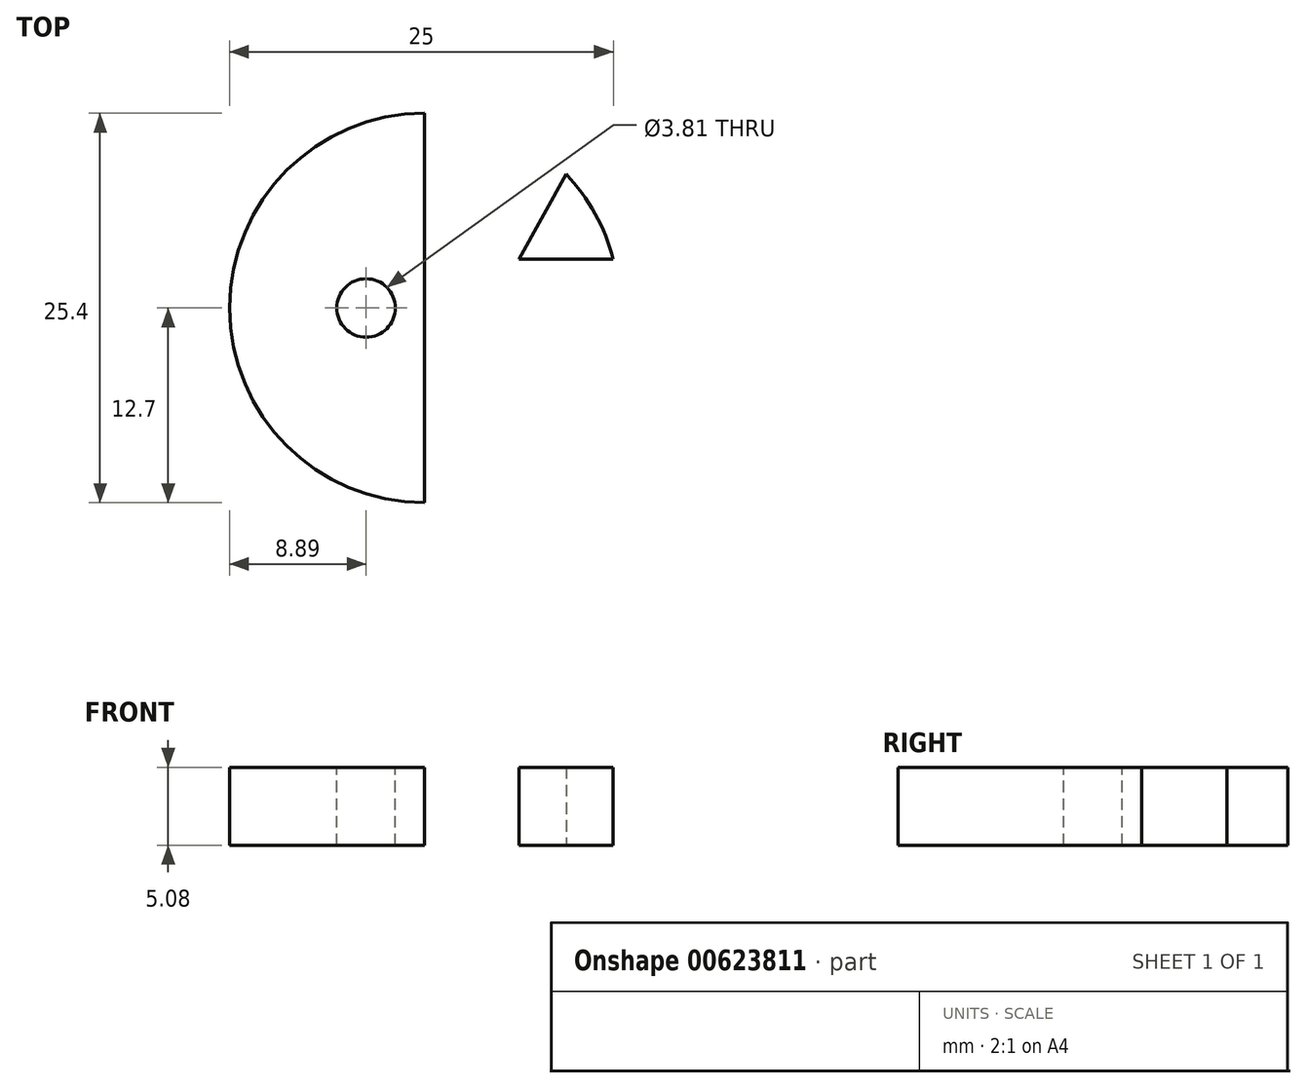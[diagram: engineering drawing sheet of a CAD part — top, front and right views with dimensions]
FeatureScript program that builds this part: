
annotation { "Feature Type Name" : "Feature", "Feature Type Description" : "" }
export const myFeature = defineFeature(function(context is Context, id is Id, definition is map)
    precondition{}
    {
        {
            var Q0;
            Q0=qCreatedBy(makeId("Top.planeOp"),FACE);
            var sketch = newSketch(context, id + "F0", { "sketchPlane" : qUnion([Q0])});
            skCircle(sketch, "E0", {"center": v(0, 0) * mm, "radius": 12.7 * mm});
            skLineSegment(sketch, "E1", {"start": v(0, 0) * mm, "end": v(0, 12.7) * mm});
            skLineSegment(sketch, "E2", {"start": v(0, 6.35) * mm, "end": v(0, 0) * mm});
            skLineSegment(sketch, "E3", {"start": v(0, 3.18) * mm, "end": v(0, 6.35) * mm});
            skLineSegment(sketch, "E4", {"start": v(0, 3.18) * mm, "end": v(12.3, 3.18) * mm});
            skLineSegment(sketch, "E5", {"start": v(-12.7, 0) * mm, "end": v(12.7, 0) * mm});
            skLineSegment(sketch, "E6.MirrorCS", {"start": v(0, -3.18) * mm, "end": v(12.3, -3.18) * mm});
            skLineSegment(sketch, "E7.MirrorCS", {"start": v(0, -6.35) * mm, "end": v(0, 0) * mm});
            skLineSegment(sketch, "E8.MirrorCS", {"start": v(0, 0) * mm, "end": v(0, -12.7) * mm});
            skLineSegment(sketch, "E9", {"start": v(6.15, 3.17) * mm, "end": v(9.22, 8.73) * mm});
            skLineSegment(sketch, "E10.MirrorCS", {"start": v(6.15, -3.17) * mm, "end": v(9.22, -8.73) * mm});
            skSolve(sketch);
        }
        {
            var Q0;
            {var subQ4=sQuery(id+"F0.wireOp",EDGE,"E2");Q0=makeQuery(id+"F0.imprint","IMPRINT",FACE,{"disambiguationData":[TD([[makeQuery(id+"F0.imprint","IMPRINT",EDGE,{"derivedFrom":subQ4}),1.0]])]});}
            var Q1;
            {var subQ1=sQuery(id+"F0.wireOp",EDGE,"E0");var subQ6=sQuery(id+"F0.wireOp",EDGE,"E5");var subQ8=makeQuery(id+"F0.imprint","INTERSECT",VERTEX,{"disambiguationData":[OD(1.0)],"derivedFrom":[subQ1,subQ6]});Q1=makeQuery(id+"F0.imprint","IMPRINT",FACE,{"disambiguationData":[TD([[makeQuery(id+"F0.imprint","IMPRINT",EDGE,{"disambiguationData":[TD([[subQ8,1.0]])],"derivedFrom":subQ1}),1.0]])]});}
            var Q2;
            {var subQ0=sQuery(id+"F0.wireOp",EDGE,"E8.MirrorCS");var subQ4=makeQuery(id+"F0.imprint","IMPRINT",VERTEX,{"derivedFrom":subQ0});Q2=makeQuery(id+"F0.imprint","IMPRINT",FACE,{"disambiguationData":[TD([[makeQuery(id+"F0.imprint","IMPRINT",EDGE,{"disambiguationData":[TD([[subQ4,1.0]])],"derivedFrom":subQ0}),-1.0]])]});}
            var Q3;
            {var subQ1=sQuery(id+"F0.wireOp",EDGE,"E1");Q3=makeQuery(id+"F0.imprint","IMPRINT",FACE,{"disambiguationData":[TD([[makeQuery(id+"F0.imprint","IMPRINT",EDGE,{"derivedFrom":subQ1}),1.0]])]});}
            var Q4;
            {var subQ3=sQuery(id+"F0.wireOp",EDGE,"E9");Q4=makeQuery(id+"F0.imprint","IMPRINT",FACE,{"disambiguationData":[TD([[makeQuery(id+"F0.imprint","IMPRINT",EDGE,{"derivedFrom":subQ3}),-1.0]])]});}
            extrude(context, id + "F1", {"entities" : qUnion([Q0, Q1, Q2, Q3, Q4]), "depth" : 5.08 * mm, "offsetDistance" : 25.4 * mm});
        }
        {
            var Q0;
            Q0=makeQuery(id+"F1.opExtrude","CAP_FACE",FACE,{"disambiguationData":[OSD([sQuery(id+"F0.wireOp",EDGE,"E0"),sQuery(id+"F0.wireOp",EDGE,"E1"),sQuery(id+"F0.wireOp",EDGE,"E3"),sQuery(id+"F0.wireOp",EDGE,"E4"),sQuery(id+"F0.wireOp",EDGE,"E6.MirrorCS"),sQuery(id+"F0.wireOp",EDGE,"E8.MirrorCS"),sQuery(id+"F0.wireOp",EDGE,"E9")])],"isStart":false});
            var sketch = newSketch(context, id + "F2", { "sketchPlane" : qUnion([Q0])});
            skCircle(sketch, "E11", {"center": v(-3.81, 0) * mm, "radius": 1.9 * mm});
            skPoint(sketch, "E12", {"position": v(-3.81, 3.18) * mm});
            skSolve(sketch);
        }
        {
            var Q0;
            Q0=makeQuery(id+"F2.imprint","IMPRINT",FACE,{"disambiguationData":[TD([[makeQuery(id+"F2.imprint","IMPRINT",EDGE,{"derivedFrom":sQuery(id+"F2.wireOp",EDGE,"E11")}),1.0]])]});
            extrude(context, id + "F3", {"entities" : qUnion([Q0]), "operationType" : NewBodyOperationType.REMOVE, "endBound" : BoundingType.THROUGH_ALL, "oppositeDirection" : true, "depth" : 12.7 * mm, "offsetDistance" : 25.4 * mm});
        }
    });
